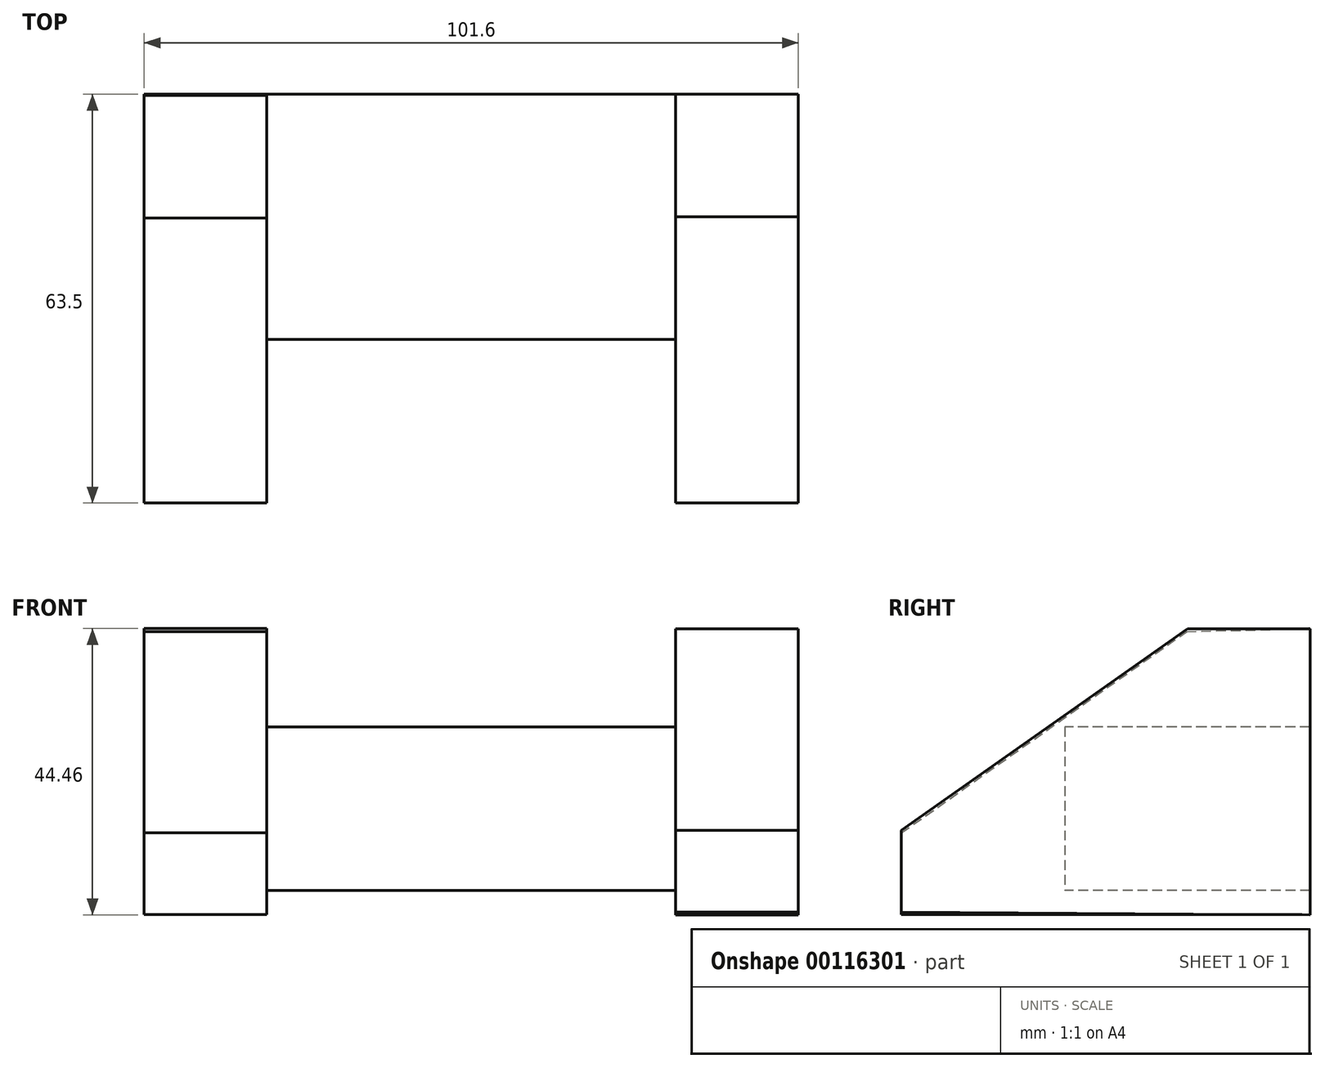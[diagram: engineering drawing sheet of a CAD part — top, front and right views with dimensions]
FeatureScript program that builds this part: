
annotation { "Feature Type Name" : "Feature", "Feature Type Description" : "" }
export const myFeature = defineFeature(function(context is Context, id is Id, definition is map)
    precondition{}
    {
        {
            var Q0;
            Q0=qCreatedBy(makeId("Top.planeOp"),FACE);
            var sketch = newSketch(context, id + "F0", { "sketchPlane" : qUnion([Q0])});
            skLineSegment(sketch, "E0.bottom", {"start": v(-32.86, 37.85) * mm, "end": v(30.64, 37.85) * mm});
            skLineSegment(sketch, "E0.top", {"start": v(-32.86, -0.25) * mm, "end": v(30.64, -0.25) * mm});
            skLineSegment(sketch, "E0.left", {"start": v(-32.86, 37.85) * mm, "end": v(-32.86, -0.25) * mm});
            skLineSegment(sketch, "E0.right", {"start": v(30.64, 37.85) * mm, "end": v(30.64, -0.25) * mm});
            skSolve(sketch);
        }
        {
            var Q0;
            Q0=makeQuery(id+"F0.imprint","IMPRINT",FACE,{"disambiguationData":[TD([[makeQuery(id+"F0.imprint","IMPRINT",EDGE,{"derivedFrom":sQuery(id+"F0.wireOp",EDGE,"E0.bottom")}),-1.0]])]});
            extrude(context, id + "F1", {"entities" : qUnion([Q0]), "depth" : 25.4 * mm});
        }
        {
            var Q0;
            Q0=makeQuery(id+"F1.opExtrude","SWEPT_FACE",FACE,{"disambiguationData":[OSD([sQuery(id+"F0.wireOp",EDGE,"E0.right")])]});
            var sketch = newSketch(context, id + "F2", { "sketchPlane" : qUnion([Q0])});
            skLineSegment(sketch, "E1", {"start": v(37.85, 0) * mm, "end": v(37.85, -3.78) * mm});
            skLineSegment(sketch, "E2", {"start": v(37.85, -3.78) * mm, "end": v(37.85, 40.67) * mm});
            skLineSegment(sketch, "E3", {"start": v(37.85, 40.67) * mm, "end": v(18.8, 40.67) * mm});
            skLineSegment(sketch, "E4", {"start": v(18.8, 40.67) * mm, "end": v(-25.65, 9.32) * mm});
            skLineSegment(sketch, "E5", {"start": v(-25.65, 9.32) * mm, "end": v(-25.65, -3.38) * mm});
            skLineSegment(sketch, "E6", {"start": v(-25.65, -3.38) * mm, "end": v(37.85, -3.78) * mm});
            skSolve(sketch);
        }
        {
            var Q0;
            Q0 = qSketchRegion(id + "F2", true);
            extrude(context, id + "F3", {"entities" : qUnion([Q0]), "operationType" : NewBodyOperationType.ADD, "depth" : 19.05 * mm});
        }
        {
            var Q0;
            Q0=makeQuery(id+"F1.opExtrude","SWEPT_FACE",FACE,{"disambiguationData":[OSD([sQuery(id+"F0.wireOp",EDGE,"E0.left")])]});
            var sketch = newSketch(context, id + "F4", { "sketchPlane" : qUnion([Q0])});
            skLineSegment(sketch, "E7", {"start": v(-37.68, 40.68) * mm, "end": v(-37.85, -3.77) * mm});
            skLineSegment(sketch, "E8", {"start": v(-37.85, -3.77) * mm, "end": v(25.65, -3.77) * mm});
            skLineSegment(sketch, "E9", {"start": v(25.65, -3.77) * mm, "end": v(25.65, 8.93) * mm});
            skLineSegment(sketch, "E10", {"start": v(25.65, 8.93) * mm, "end": v(-18.63, 40.21) * mm});
            skLineSegment(sketch, "E11", {"start": v(-18.63, 40.21) * mm, "end": v(-37.68, 40.68) * mm});
            skSolve(sketch);
        }
        {
            var Q0;
            Q0 = qSketchRegion(id + "F4", true);
            extrude(context, id + "F5", {"entities" : qUnion([Q0]), "operationType" : NewBodyOperationType.ADD, "depth" : 19.05 * mm});
        }
    });
